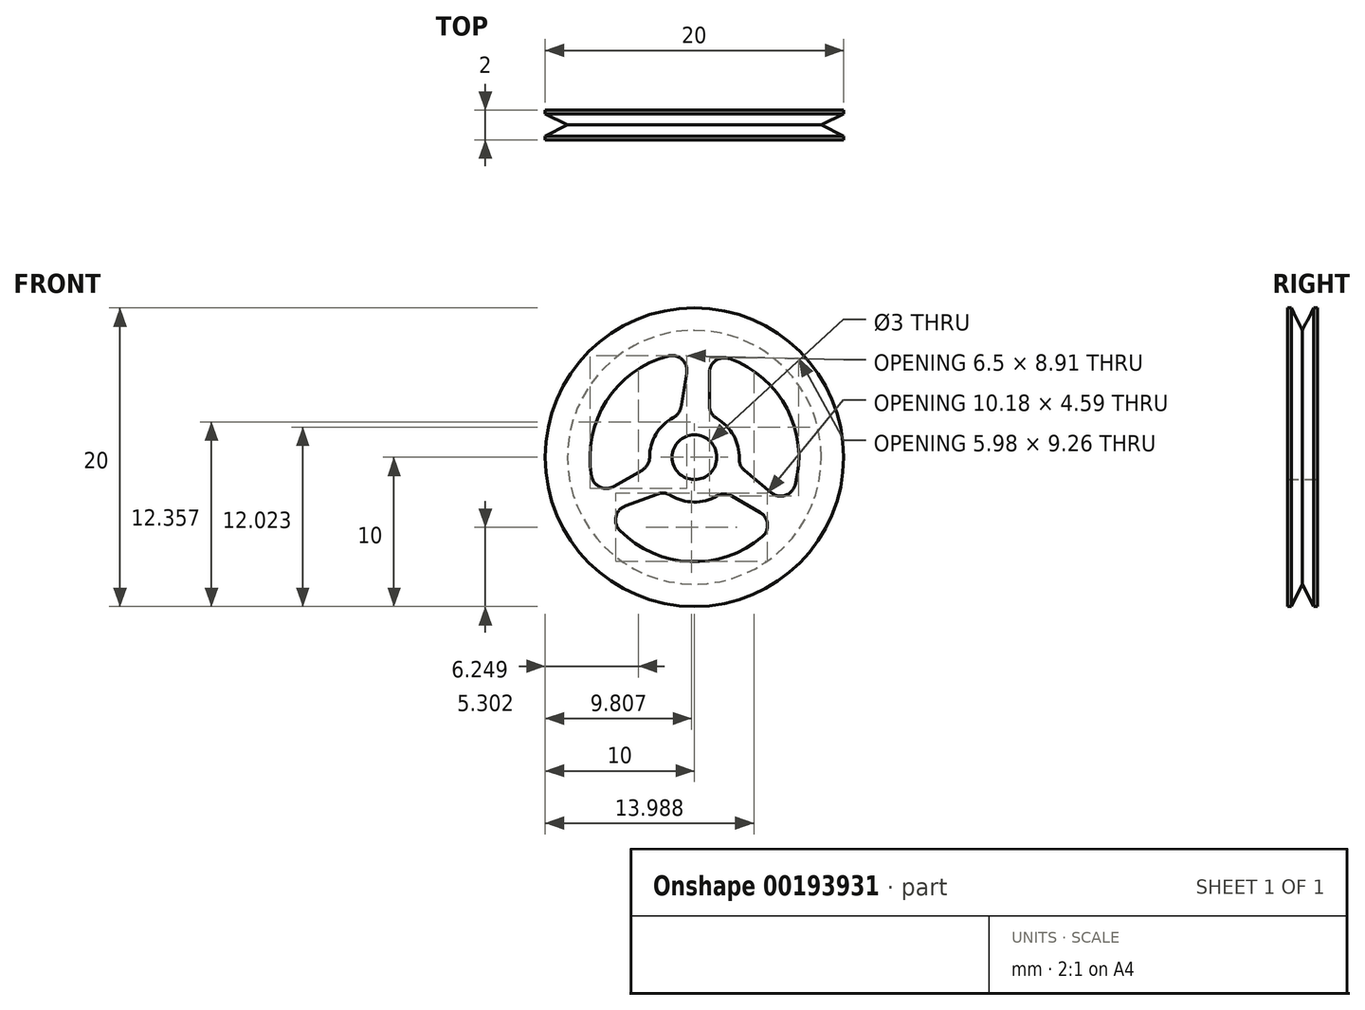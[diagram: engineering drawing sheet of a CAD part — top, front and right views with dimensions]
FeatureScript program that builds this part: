
annotation { "Feature Type Name" : "Feature", "Feature Type Description" : "" }
export const myFeature = defineFeature(function(context is Context, id is Id, definition is map)
    precondition{}
    {
        {
            var Q0;
            Q0=qCreatedBy(makeId("Front.planeOp"),FACE);
            var sketch = newSketch(context, id + "F0", { "sketchPlane" : qUnion([Q0])});
            skCircle(sketch, "E0", {"center": v(0, 0) * mm, "radius": 10 * mm});
            skArc(sketch, "E1.0", {"start": v(-5, -4.9) * mm, "mid": v(-0.3, -7) * mm, "end": v(4.55, -5.32) * mm});
            skArc(sketch, "E2", {"start": v(-1.42, 2.64) * mm, "mid": v(-2.58, 1.54) * mm, "end": v(-3, 0) * mm});
            skCircle(sketch, "E3", {"center": v(0, 0) * mm, "radius": 1.5 * mm});
            skLineSegment(sketch, "E4.0", {"start": v(0.24, 10) * mm, "end": v(0.24, 10) * mm});
            skLineSegment(sketch, "E5.0", {"start": v(1, 10) * mm, "end": v(1, 9.95) * mm});
            skLineSegment(sketch, "E6.trimOffspring", {"start": v(-0.51, 5.64) * mm, "end": v(-0.9, 3.35) * mm});
            skLineSegment(sketch, "E7.trimOffspring", {"start": v(1, 5.66) * mm, "end": v(1, 3.46) * mm});
            skLineSegment(sketch, "E8.1.0", {"start": v(-5.4, -1.96) * mm, "end": v(-3.5, -0.87) * mm});
            skLineSegment(sketch, "E8.1.1", {"start": v(-4.63, -3.26) * mm, "end": v(-2.45, -2.46) * mm});
            skLineSegment(sketch, "E8.2.0", {"start": v(4.4, -3.7) * mm, "end": v(2.5, -2.6) * mm});
            skLineSegment(sketch, "E8.2.1", {"start": v(5.14, -2.37) * mm, "end": v(3.36, -0.89) * mm});
            skArc(sketch, "E9.trimOffspring", {"start": v(-1.58, -2.55) * mm, "mid": v(-0.05, -3) * mm, "end": v(1.5, -2.6) * mm});
            skArc(sketch, "E10.trimOffspring", {"start": v(3, -0.1) * mm, "mid": v(2.62, 1.46) * mm, "end": v(1.5, 2.6) * mm});
            skArc(sketch, "E11.trimOffspring", {"start": v(6.74, -1.87) * mm, "mid": v(6.2, 3.23) * mm, "end": v(2.33, 6.6) * mm});
            skArc(sketch, "E12.trimOffspring", {"start": v(-1.75, 6.78) * mm, "mid": v(-5.9, 3.76) * mm, "end": v(-6.88, -1.28) * mm});
            skPoint(sketch, "E13.visualSharp", {"position": v(-0.28, 7) * mm});
            skArc(sketch, "E13.filletArc", {"start": v(-0.51, 5.64) * mm, "mid": v(-0.82, 6.54) * mm, "end": v(-1.75, 6.78) * mm});
            skPoint(sketch, "E14.visualSharp", {"position": v(-1, 2.83) * mm});
            skArc(sketch, "E14.filletArc", {"start": v(-1.42, 2.64) * mm, "mid": v(-1.08, 2.94) * mm, "end": v(-0.9, 3.35) * mm});
            skPoint(sketch, "E15.visualSharp", {"position": v(-2.95, -0.55) * mm});
            skArc(sketch, "E15.filletArc", {"start": v(-3.5, -0.87) * mm, "mid": v(-3.13, -0.5) * mm, "end": v(-3, 0) * mm});
            skPoint(sketch, "E16.visualSharp", {"position": v(-6.5, -2.6) * mm});
            skArc(sketch, "E16.filletArc", {"start": v(-6.88, -1.28) * mm, "mid": v(-6.32, -2) * mm, "end": v(-5.4, -1.96) * mm});
            skPoint(sketch, "E17.visualSharp", {"position": v(-5.92, -3.74) * mm});
            skArc(sketch, "E17.filletArc", {"start": v(-4.63, -3.26) * mm, "mid": v(-5.26, -3.98) * mm, "end": v(-5, -4.9) * mm});
            skPoint(sketch, "E18.visualSharp", {"position": v(-1.95, -2.28) * mm});
            skArc(sketch, "E18.filletArc", {"start": v(-1.58, -2.55) * mm, "mid": v(-2, -2.4) * mm, "end": v(-2.45, -2.46) * mm});
            skPoint(sketch, "E19.visualSharp", {"position": v(1.95, -2.28) * mm});
            skArc(sketch, "E19.filletArc", {"start": v(2.5, -2.6) * mm, "mid": v(2, -2.46) * mm, "end": v(1.5, -2.6) * mm});
            skPoint(sketch, "E20.visualSharp", {"position": v(5.5, -4.33) * mm});
            skArc(sketch, "E20.filletArc", {"start": v(4.55, -5.32) * mm, "mid": v(4.9, -4.47) * mm, "end": v(4.4, -3.7) * mm});
            skPoint(sketch, "E21.visualSharp", {"position": v(2.95, -0.55) * mm});
            skArc(sketch, "E21.filletArc", {"start": v(3, -0.1) * mm, "mid": v(3.09, -0.53) * mm, "end": v(3.36, -0.89) * mm});
            skPoint(sketch, "E22.visualSharp", {"position": v(6.2, -3.26) * mm});
            skArc(sketch, "E22.filletArc", {"start": v(5.14, -2.37) * mm, "mid": v(6.08, -2.56) * mm, "end": v(6.74, -1.87) * mm});
            skPoint(sketch, "E23.visualSharp", {"position": v(1, 6.93) * mm});
            skArc(sketch, "E23.filletArc", {"start": v(2.33, 6.6) * mm, "mid": v(1.42, 6.47) * mm, "end": v(1, 5.66) * mm});
            skPoint(sketch, "E24.visualSharp", {"position": v(1, 2.83) * mm});
            skArc(sketch, "E24.filletArc", {"start": v(1, 3.46) * mm, "mid": v(1.13, 2.96) * mm, "end": v(1.5, 2.6) * mm});
            skSolve(sketch);
        }
        {
            var Q0;
            Q0=makeQuery(id+"F0.imprint","IMPRINT",FACE,{"disambiguationData":[TD([[makeQuery(id+"F0.imprint","IMPRINT",EDGE,{"derivedFrom":sQuery(id+"F0.wireOp",EDGE,"E0")}),1.0]])]});
            extrude(context, id + "F1", {"entities" : qUnion([Q0]), "depth" : 2 * mm, "symmetric" : true});
        }
        {
            var Q0;
            Q0=qCreatedBy(makeId("Right.planeOp"),FACE);
            var sketch = newSketch(context, id + "F2", { "sketchPlane" : qUnion([Q0])});
            skLineSegment(sketch, "E25", {"start": v(0, 8.5) * mm, "end": v(0, 10) * mm});
            skLineSegment(sketch, "E26", {"start": v(0, 10) * mm, "end": v(-0.75, 10) * mm});
            skLineSegment(sketch, "E27", {"start": v(-0.75, 10) * mm, "end": v(0, 8.5) * mm});
            skLineSegment(sketch, "E28.MirrorCS", {"start": v(0, 10) * mm, "end": v(0.75, 10) * mm});
            skLineSegment(sketch, "E29.MirrorCS", {"start": v(0.75, 10) * mm, "end": v(0, 8.5) * mm});
            skLineSegment(sketch, "E30", {"start": v(-27.48, 0) * mm, "end": v(37.03, 0) * mm, "construction": true});
            skLineSegment(sketch, "E31", {"start": v(-0.75, 10) * mm, "end": v(0, 10) * mm});
            skLineSegment(sketch, "E32", {"start": v(0.75, 10) * mm, "end": v(0, 10) * mm});
            skSolve(sketch);
        }
        {
            var Q0;
            Q0 = qSketchRegion(id + "F2", true);
            var Q1;
            Q1=sQuery(id+"F2.wireOp",EDGE,"E30");
            revolve(context, id + "F3", {"operationType" : NewBodyOperationType.REMOVE, "entities" : qUnion([Q0]), "axis" : qUnion([Q1]), "revolveType" : RevolveType.FULL, "oppositeDirection" : true});
        }
    });
